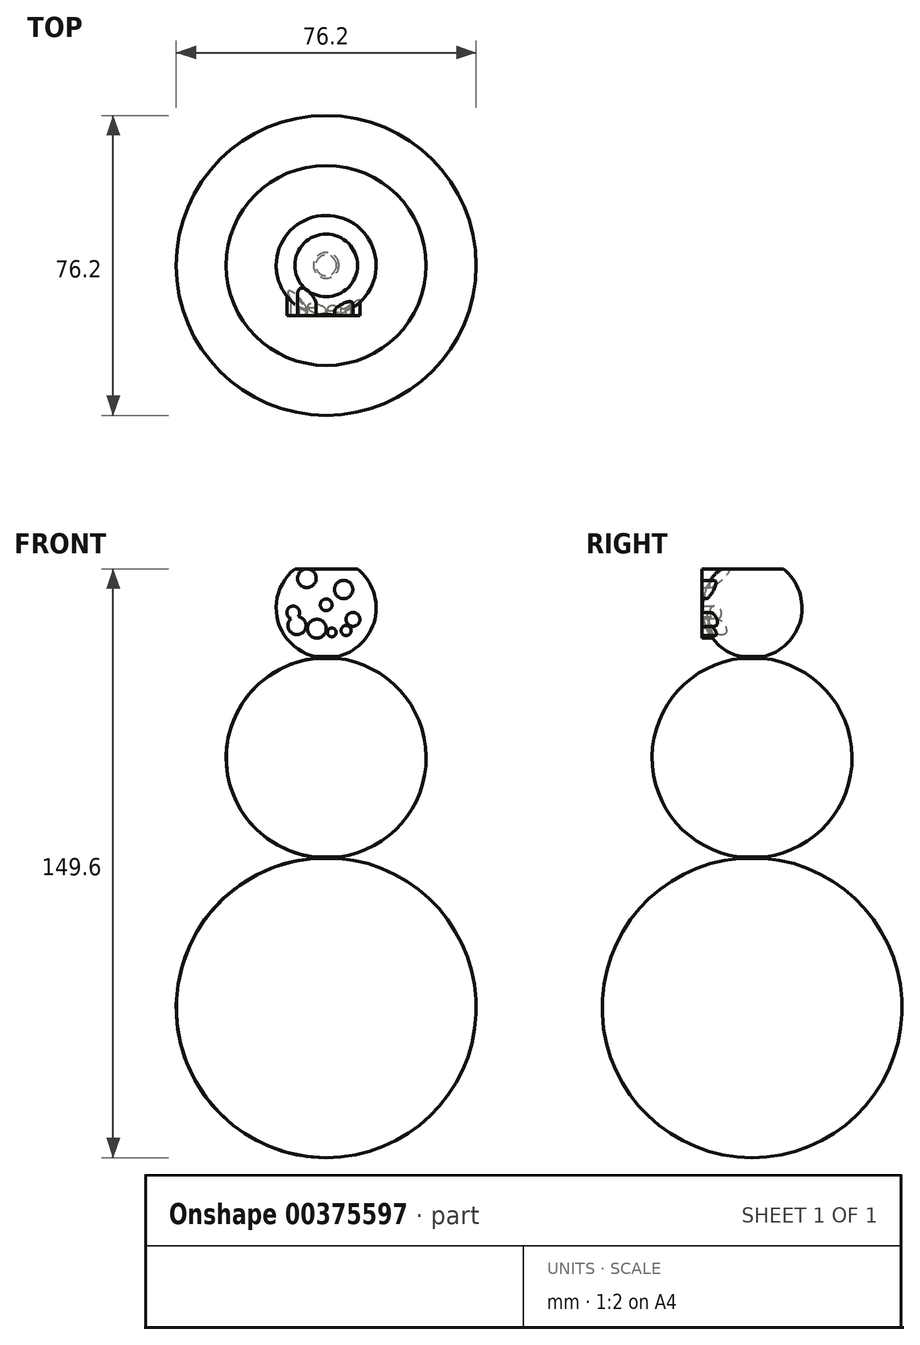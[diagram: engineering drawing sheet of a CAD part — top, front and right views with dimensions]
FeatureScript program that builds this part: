
annotation { "Feature Type Name" : "Feature", "Feature Type Description" : "" }
export const myFeature = defineFeature(function(context is Context, id is Id, definition is map)
    precondition{}
    {
        {
            var Q0;
            Q0=qCreatedBy(makeId("Front.planeOp"),FACE);
            var sketch = newSketch(context, id + "F0", { "sketchPlane" : qUnion([Q0])});
            skArc(sketch, "E0", {"start": v(0, -38.1) * mm, "mid": v(38.1, 0) * mm, "end": v(0, 38.1) * mm});
            skLineSegment(sketch, "E1", {"start": v(0, 0) * mm, "end": v(0, 63.5) * mm});
            skArc(sketch, "E2", {"start": v(0, 38.1) * mm, "mid": v(25.4, 63.5) * mm, "end": v(0, 88.9) * mm});
            skLineSegment(sketch, "E3", {"start": v(0, 63.5) * mm, "end": v(0, 101.6) * mm});
            skArc(sketch, "E4", {"start": v(0, 88.9) * mm, "mid": v(11.98, 97.38) * mm, "end": v(7.96, 111.5) * mm});
            skLineSegment(sketch, "E5", {"start": v(2.63, 89.18) * mm, "end": v(2.63, 88.76) * mm});
            skLineSegment(sketch, "E6", {"start": v(3.25, 38.3) * mm, "end": v(3.25, 37.96) * mm});
            skLineSegment(sketch, "E7", {"start": v(0, 101.6) * mm, "end": v(0, 111.5) * mm});
            skLineSegment(sketch, "E8", {"start": v(0, 0) * mm, "end": v(0, -38.1) * mm});
            skLineSegment(sketch, "E9", {"start": v(0, 111.5) * mm, "end": v(7.96, 111.5) * mm});
            skSolve(sketch);
        }
        {
            var Q0;
            {var subQ3=sQuery(id+"F0.wireOp",EDGE,"E7");Q0=makeQuery(id+"F0.imprint","IMPRINT",FACE,{"disambiguationData":[TD([[makeQuery(id+"F0.imprint","IMPRINT",EDGE,{"derivedFrom":subQ3}),-1.0]])]});}
            var Q1;
            {var subQ1=sQuery(id+"F0.wireOp",EDGE,"E2");var subQ3=makeQuery(id+"F0.imprint","INTERSECT",VERTEX,{"derivedFrom":[subQ1,sQuery(id+"F0.wireOp",EDGE,"E5")]});Q1=makeQuery(id+"F0.imprint","IMPRINT",FACE,{"disambiguationData":[TD([[makeQuery(id+"F0.imprint","IMPRINT",EDGE,{"disambiguationData":[TD([[subQ3,1.0]])],"derivedFrom":subQ1}),1.0]])]});}
            var Q2;
            {var subQ0=sQuery(id+"F0.wireOp",EDGE,"E8");Q2=makeQuery(id+"F0.imprint","IMPRINT",FACE,{"disambiguationData":[TD([[makeQuery(id+"F0.imprint","IMPRINT",EDGE,{"derivedFrom":subQ0}),1.0]])]});}
            var Q3;
            {var subQ3=sQuery(id+"F0.wireOp",EDGE,"E6");Q3=makeQuery(id+"F0.imprint","IMPRINT",FACE,{"disambiguationData":[TD([[makeQuery(id+"F0.imprint","IMPRINT",EDGE,{"derivedFrom":subQ3}),-1.0]])]});}
            var Q4;
            {var subQ3=sQuery(id+"F0.wireOp",EDGE,"E5");Q4=makeQuery(id+"F0.imprint","IMPRINT",FACE,{"disambiguationData":[TD([[makeQuery(id+"F0.imprint","IMPRINT",EDGE,{"derivedFrom":subQ3}),-1.0]])]});}
            var Q5;
            Q5=sQuery(id+"F0.wireOp",EDGE,"E3");
            revolve(context, id + "F1", {"entities" : qUnion([Q0, Q1, Q2, Q3, Q4]), "axis" : qUnion([Q5]), "revolveType" : RevolveType.FULL});
        }
        {
            var Q0;
            Q0=qCreatedBy(makeId("Front.planeOp"),FACE);
            var sketch = newSketch(context, id + "F2", { "sketchPlane" : qUnion([Q0])});
            skCircle(sketch, "E10", {"center": v(4.44, 106.26) * mm, "radius": 2.33 * mm});
            skCircle(sketch, "E11", {"center": v(-4.9, 109.1) * mm, "radius": 2.38 * mm});
            skCircle(sketch, "E12", {"center": v(5.07, 95.83) * mm, "radius": 1.27 * mm});
            skCircle(sketch, "E13", {"center": v(1.43, 95.35) * mm, "radius": 1.12 * mm});
            skCircle(sketch, "E14", {"center": v(-2.36, 96.3) * mm, "radius": 2.4 * mm});
            skCircle(sketch, "E15", {"center": v(-7.42, 97.1) * mm, "radius": 2.3 * mm});
            skCircle(sketch, "E16", {"center": v(6.8, 98.67) * mm, "radius": 1.77 * mm});
            skCircle(sketch, "E17", {"center": v(-8.37, 100.41) * mm, "radius": 1.63 * mm});
            skSolve(sketch);
        }
        {
            var Q0;
            Q0 = qSketchRegion(id + "F2", true);
            extrude(context, id + "F3", {"entities" : qUnion([Q0]), "operationType" : NewBodyOperationType.ADD, "depth" : 12.7 * mm});
        }
        {
            var Q0;
            Q0=qCreatedBy(makeId("Front.planeOp"),FACE);
            var sketch = newSketch(context, id + "F4", { "sketchPlane" : qUnion([Q0])});
            skCircle(sketch, "E18", {"center": v(0, 102.35) * mm, "radius": 1.5 * mm});
            skSolve(sketch);
        }
        {
            var Q0;
            Q0 = qSketchRegion(id + "F4", true);
            extrude(context, id + "F5", {"entities" : qUnion([Q0]), "operationType" : NewBodyOperationType.ADD, "depth" : 12.7 * mm});
        }
    });
